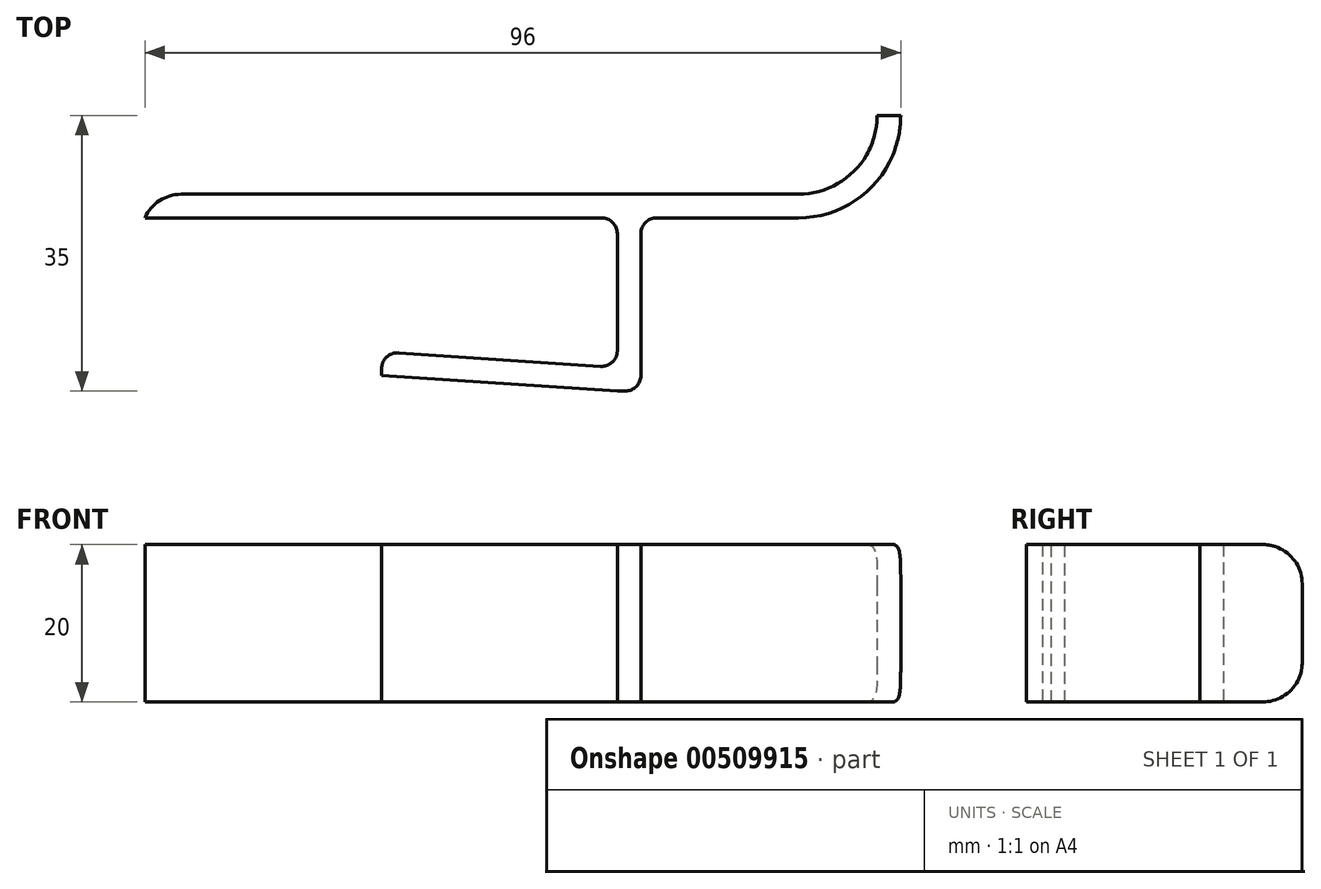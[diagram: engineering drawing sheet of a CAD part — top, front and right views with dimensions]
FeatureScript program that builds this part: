
annotation { "Feature Type Name" : "Feature", "Feature Type Description" : "" }
export const myFeature = defineFeature(function(context is Context, id is Id, definition is map)
    precondition{}
    {
        {
            var Q0;
            Q0=qCreatedBy(makeId("Top.planeOp"),FACE);
            var sketch = newSketch(context, id + "F0", { "sketchPlane" : qUnion([Q0])});
            skLineSegment(sketch, "E0.bottom", {"start": v(-60, 3) * mm, "end": v(23, 3) * mm});
            skLineSegment(sketch, "E0.top", {"start": v(-60, 0) * mm, "end": v(23, 0) * mm});
            skLineSegment(sketch, "E0.left", {"start": v(-60, 3) * mm, "end": v(-60, 0) * mm});
            skLineSegment(sketch, "E1.bottom", {"start": v(0, 0) * mm, "end": v(3, 0) * mm});
            skLineSegment(sketch, "E1.top", {"start": v(0, -22) * mm, "end": v(3, -22) * mm});
            skLineSegment(sketch, "E1.left", {"start": v(0, 0) * mm, "end": v(0, -22) * mm});
            skLineSegment(sketch, "E1.right", {"start": v(3, 0) * mm, "end": v(3, -22) * mm});
            skLineSegment(sketch, "E2.bottom", {"start": v(0, -22) * mm, "end": v(-29.93, -20) * mm});
            skLineSegment(sketch, "E2.top", {"start": v(0.02, -19) * mm, "end": v(-29.91, -17) * mm});
            skLineSegment(sketch, "E2.left", {"start": v(0, -22) * mm, "end": v(0.02, -19) * mm});
            skLineSegment(sketch, "E2.right", {"start": v(-29.93, -20) * mm, "end": v(-29.91, -17) * mm});
            skArc(sketch, "E3", {"start": v(23, 3) * mm, "mid": v(30.07, 5.93) * mm, "end": v(33, 13) * mm});
            skArc(sketch, "E4", {"start": v(23, 0) * mm, "mid": v(32.2, 3.8) * mm, "end": v(36, 13) * mm});
            skLineSegment(sketch, "E5", {"start": v(33, 13) * mm, "end": v(36, 13) * mm});
            skSolve(sketch);
        }
        {
            var Q0;
            Q0 = qSketchRegion(id + "F0", true);
            extrude(context, id + "F1", {"entities" : qUnion([Q0]), "depth" : 20 * mm});
        }
        {
            var Q0;
            Q0=makeQuery(id+"F1.opExtrude","CAP_EDGE",EDGE,{"disambiguationData":[OSD([sQuery(id+"F0.wireOp",EDGE,"E5")])],"isStart":false});
            var Q1;
            Q1=makeQuery(id+"F1.opExtrude","CAP_EDGE",EDGE,{"disambiguationData":[OSD([sQuery(id+"F0.wireOp",EDGE,"E5")])],"isStart":true});
            var Q2;
            Q2=makeQuery(id+"F1.opExtrude","SWEPT_EDGE",EDGE,{"disambiguationData":[OSD([sQuery(id+"F0.wireOp",EDGE,"E0.bottom"),sQuery(id+"F0.wireOp",EDGE,"E0.left")])]});
            fillet(context, id + "F2", {"entities" : qUnion([Q0, Q1, Q2]), "radius" : 5 * mm, "tangentPropagation" : true, "allowEdgeOverflow" : false});
        }
        {
            var Q0;
            Q0=makeQuery(id+"F1.opExtrude","SWEPT_EDGE",EDGE,{"disambiguationData":[OSD([sQuery(id+"F0.wireOp",EDGE,"E2.top"),sQuery(id+"F0.wireOp",EDGE,"E2.right")])]});
            var Q1;
            Q1=makeQuery(id+"F1.opExtrude","SWEPT_EDGE",EDGE,{"disambiguationData":[OSD([sQuery(id+"F0.wireOp",EDGE,"E1.left"),sQuery(id+"F0.wireOp",EDGE,"E2.top")])]});
            var Q2;
            Q2=makeQuery(id+"F1.opExtrude","SWEPT_EDGE",EDGE,{"disambiguationData":[OSD([sQuery(id+"F0.wireOp",EDGE,"E1.top"),sQuery(id+"F0.wireOp",EDGE,"E1.right")])]});
            var Q3;
            Q3=makeQuery(id+"F1.opExtrude","SWEPT_EDGE",EDGE,{"disambiguationData":[OSD([sQuery(id+"F0.wireOp",EDGE,"E0.top"),sQuery(id+"F0.wireOp",EDGE,"E1.bottom"),sQuery(id+"F0.wireOp",EDGE,"E1.right")])]});
            var Q4;
            Q4=makeQuery(id+"F1.opExtrude","SWEPT_EDGE",EDGE,{"disambiguationData":[OSD([sQuery(id+"F0.wireOp",EDGE,"E0.top"),sQuery(id+"F0.wireOp",EDGE,"E1.bottom"),sQuery(id+"F0.wireOp",EDGE,"E1.left")])]});
            fillet(context, id + "F3", {"entities" : qUnion([Q0, Q1, Q2, Q3, Q4]), "radius" : 2 * mm, "tangentPropagation" : true, "allowEdgeOverflow" : false});
        }
    });
